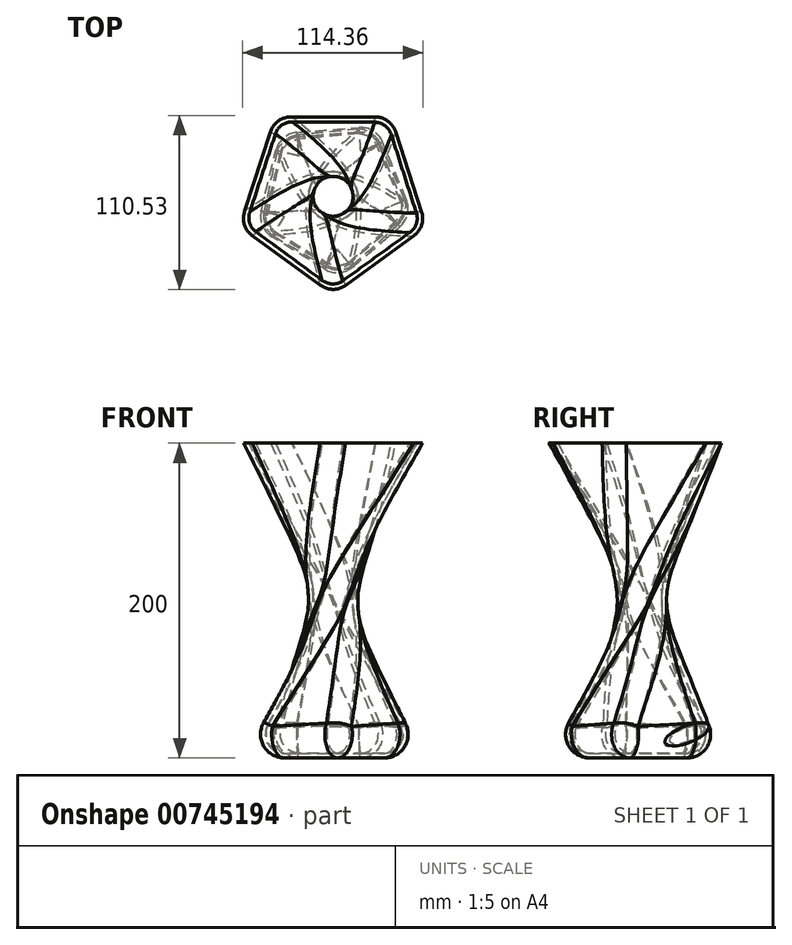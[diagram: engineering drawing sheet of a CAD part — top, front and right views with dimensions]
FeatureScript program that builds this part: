
annotation { "Feature Type Name" : "Feature", "Feature Type Description" : "" }
export const myFeature = defineFeature(function(context is Context, id is Id, definition is map)
    precondition{}
    {
        {
            var Q0;
            Q0=qCreatedBy(makeId("Top.planeOp"),FACE);
            var sketch = newSketch(context, id + "F0", { "sketchPlane" : qUnion([Q0])});
            skCircle(sketch, "E0.cCircle", {"center": v(0, 0) * mm, "radius": 50.44 * mm, "construction": true});
            skLineSegment(sketch, "E0.0", {"start": v(-36.65, 50.44) * mm, "end": v(36.65, 50.44) * mm});
            skLineSegment(sketch, "E0.1", {"start": v(36.65, 50.44) * mm, "end": v(59.3, -19.27) * mm});
            skLineSegment(sketch, "E0.2", {"start": v(59.3, -19.27) * mm, "end": v(0, -62.35) * mm});
            skLineSegment(sketch, "E0.3", {"start": v(0, -62.35) * mm, "end": v(-59.3, -19.27) * mm});
            skLineSegment(sketch, "E0.4", {"start": v(-59.3, -19.27) * mm, "end": v(-36.65, 50.44) * mm});
            skPoint(sketch, "E0.0.midPoint", {"position": v(0, 50.44) * mm});
            skSolve(sketch);
        }
        {
            var Q0;
            Q0=qCreatedBy(makeId("Top.planeOp"),FACE);
            cPlane(context, id + "F1", {"entities" : qUnion([Q0]), "cplaneType" : CPlaneType.OFFSET, "offset" : 200 * mm, "width" : 150 * mm, "height" : 150 * mm});
        }
        {
            var Q0;
            Q0=qCreatedBy(id+"F1.planeOp",FACE);
            var sketch = newSketch(context, id + "F2", { "sketchPlane" : qUnion([Q0])});
            skLineSegment(sketch, "E1.0", {"start": v(-59.3, -19.27) * mm, "end": v(-36.65, 50.44) * mm});
            skLineSegment(sketch, "E2.0", {"start": v(-36.65, 50.44) * mm, "end": v(36.65, 50.44) * mm});
            skLineSegment(sketch, "E3.0", {"start": v(36.65, 50.44) * mm, "end": v(59.3, -19.27) * mm});
            skLineSegment(sketch, "E4.0", {"start": v(59.3, -19.27) * mm, "end": v(0, -62.35) * mm});
            skLineSegment(sketch, "E5.0", {"start": v(0, -62.35) * mm, "end": v(-59.3, -19.27) * mm});
            skSolve(sketch);
        }
        {
            var Q0;
            Q0=makeQuery(id+"F0.imprint","IMPRINT",FACE,{"disambiguationData":[TD([[makeQuery(id+"F0.imprint","IMPRINT",EDGE,{"derivedFrom":sQuery(id+"F0.wireOp",EDGE,"E0.0")}),-1.0]])]});
            var Q1;
            Q1=makeQuery(id+"F2.imprint","IMPRINT",FACE,{"disambiguationData":[TD([[makeQuery(id+"F2.imprint","IMPRINT",EDGE,{"derivedFrom":sQuery(id+"F2.wireOp",EDGE,"E1.0")}),-1.0]])]});
            var Q2;
            Q2=sQuery(id+"F2.wireOp",VERTEX,"E1.0.start");
            var Q3;
            Q3=sQuery(id+"F0.wireOp",VERTEX,"E0.1.start");
            loft(context, id + "F3", {"sheetProfilesArray" : [{ "sheetProfileEntities" : qUnion([Q0]) }, { "sheetProfileEntities" : qUnion([Q1]) }], "matchConnections" : true, "connections" : [{ "connectionEntities" : qUnion([Q2, Q3]), "connectionEdgeQueries" : qUnion([]), "connectionEdgeParameters" : [] }]});
        }
        {
            var Q0;
            Q0=makeQuery(id+"F3.opLoft","SWEPT_EDGE",EDGE,{"disambiguationData":[OSD([sQuery(id+"F0.wireOp",EDGE,"E0.0"),sQuery(id+"F0.wireOp",EDGE,"E0.4"),sQuery(id+"F2.wireOp",EDGE,"E4.0"),sQuery(id+"F2.wireOp",EDGE,"E5.0")])]});
            var Q1;
            Q1=makeQuery(id+"F3.opLoft","SWEPT_EDGE",EDGE,{"disambiguationData":[OSD([sQuery(id+"F0.wireOp",EDGE,"E0.3"),sQuery(id+"F0.wireOp",EDGE,"E0.4"),sQuery(id+"F2.wireOp",EDGE,"E3.0"),sQuery(id+"F2.wireOp",EDGE,"E4.0")])]});
            var Q2;
            Q2=makeQuery(id+"F3.opLoft","SWEPT_EDGE",EDGE,{"disambiguationData":[OSD([sQuery(id+"F0.wireOp",EDGE,"E0.0"),sQuery(id+"F0.wireOp",EDGE,"E0.1"),sQuery(id+"F2.wireOp",EDGE,"E1.0"),sQuery(id+"F2.wireOp",EDGE,"E5.0")])]});
            var Q3;
            Q3=makeQuery(id+"F3.opLoft","SWEPT_EDGE",EDGE,{"disambiguationData":[OSD([sQuery(id+"F0.wireOp",EDGE,"E0.1"),sQuery(id+"F0.wireOp",EDGE,"E0.2"),sQuery(id+"F2.wireOp",EDGE,"E1.0"),sQuery(id+"F2.wireOp",EDGE,"E2.0")])]});
            var Q4;
            Q4=makeQuery(id+"F3.opLoft","SWEPT_EDGE",EDGE,{"disambiguationData":[OSD([sQuery(id+"F0.wireOp",EDGE,"E0.2"),sQuery(id+"F0.wireOp",EDGE,"E0.3"),sQuery(id+"F2.wireOp",EDGE,"E2.0"),sQuery(id+"F2.wireOp",EDGE,"E3.0")])]});
            fillet(context, id + "F4", {"entities" : qUnion([Q0, Q1, Q2, Q3, Q4]), "radius" : 15 * mm, "tangentPropagation" : true, "allowEdgeOverflow" : false});
        }
        {
            var Q0;
            Q0=makeQuery(id+"F3.opLoft","MID_CAP_EDGE",EDGE,{"disambiguationData":[OSD([sQuery(id+"F0.wireOp",EDGE,"E0.0"),sQuery(id+"F0.wireOp",EDGE,"E0.1"),sQuery(id+"F0.wireOp",EDGE,"E0.4")])],"capPos":0.0});
            fillet(context, id + "F5", {"entities" : qUnion([Q0]), "radius" : 15 * mm, "tangentPropagation" : true, "allowEdgeOverflow" : false});
        }
        {
            var Q0;
            Q0=makeQuery(id+"F3.opLoft","CAP_FACE",FACE,{"disambiguationData":[OSD([makeQuery(id+"F2.imprint","IMPRINT",FACE,{"disambiguationData":[TD([[makeQuery(id+"F2.imprint","IMPRINT",EDGE,{"derivedFrom":sQuery(id+"F2.wireOp",EDGE,"E1.0")}),-1.0]])]})])],"isStart":true});
            shell(context, id + "F6", {"entities" : qUnion([Q0]), "thickness" : 3 * mm});
        }
    });
